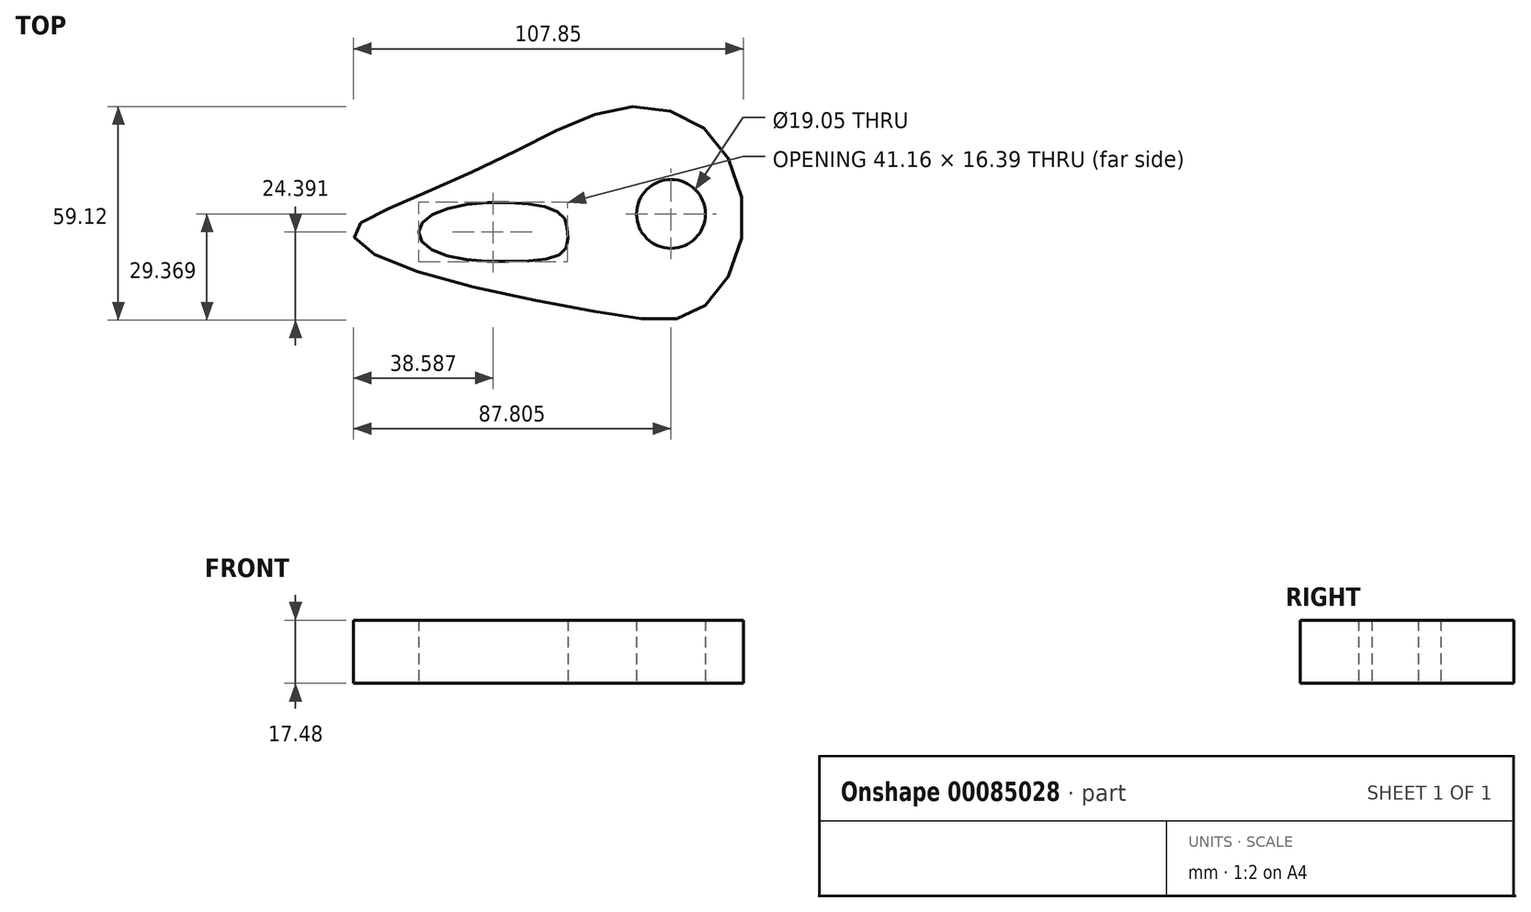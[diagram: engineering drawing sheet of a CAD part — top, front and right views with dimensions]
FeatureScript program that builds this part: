
annotation { "Feature Type Name" : "Feature", "Feature Type Description" : "" }
export const myFeature = defineFeature(function(context is Context, id is Id, definition is map)
    precondition{}
    {
        {
            var Q0;
            Q0=qCreatedBy(makeId("Top.planeOp"),FACE);
            var sketch = newSketch(context, id + "F0", { "sketchPlane" : qUnion([Q0])});
            skFitSpline(sketch, "E0", {"points": [v(-35.81, 6.55) * mm, v(0, 22.7) * mm, v(29.72, 34.6) * mm, v(53.19, 26.97) * mm, v(62.03, 0) * mm, v(49.53, -21.8) * mm, v(25.45, -22.7) * mm, v(-34.9, -8.38) * mm, v(-45.57, 0) * mm, v(-35.81, 6.55) * mm]});
            skSolve(sketch);
        }
        {
            var Q0;
            Q0=makeQuery(id+"F0.imprint","IMPRINT",FACE,{"disambiguationData":[TD([[makeQuery(id+"F0.imprint","IMPRINT",EDGE,{"derivedFrom":sQuery(id+"F0.wireOp",EDGE,"E0")}),-1.0]])]});
            extrude(context, id + "F1", {"entities" : qUnion([Q0]), "depth" : 17.48 * mm});
        }
        {
            var Q0;
            Q0=qCreatedBy(makeId("Top.planeOp"),FACE);
            var sketch = newSketch(context, id + "F2", { "sketchPlane" : qUnion([Q0])});
            skCircle(sketch, "E1", {"center": v(42.21, 5.03) * mm, "radius": 8.13 * mm});
            skSolve(sketch);
        }
        {
            var Q0;
            Q0=sQuery(id+"F2.wireOp",VERTEX,"E1.center");
            var Q1;
            Q1=makeQuery(id+"F1.opExtrude","SWEPT_BODY",BODY,{"disambiguationData":[OSD([sQuery(id+"F0.wireOp",EDGE,"E0")])]});
            hole(context, id + "F3", {"style" : HoleStyle.SIMPLE, "endStyle" : HoleEndStyle.THROUGH, "oppositeDirection" : true, "holeDiameter" : 19.05 * mm, "locations" : qUnion([Q0]), "scope" : qUnion([Q1]), "isTappedThrough" : true});
        }
        {
            var Q0;
            Q0=makeQuery(id+"F1.opExtrude","CAP_FACE",FACE,{"disambiguationData":[OSD([sQuery(id+"F0.wireOp",EDGE,"E0")])],"isStart":false});
            var sketch = newSketch(context, id + "F4", { "sketchPlane" : qUnion([Q0])});
            skFitSpline(sketch, "E2", {"points": [v(-27.58, 0) * mm, v(-22.1, 5.64) * mm, v(0, 8.08) * mm, v(12.04, 4.72) * mm, v(13.56, 0) * mm, v(12.65, -5.33) * mm, v(0, -8.08) * mm, v(-22.4, -5.64) * mm, v(-27.58, 0) * mm]});
            skSolve(sketch);
        }
        {
            var Q0;
            Q0=makeQuery(id+"F4.imprint","IMPRINT",FACE,{"disambiguationData":[TD([[makeQuery(id+"F4.imprint","IMPRINT",EDGE,{"derivedFrom":sQuery(id+"F4.wireOp",EDGE,"E2")}),-1.0]])]});
            extrude(context, id + "F5", {"entities" : qUnion([Q0]), "operationType" : NewBodyOperationType.REMOVE, "oppositeDirection" : true, "depth" : 25.4 * mm});
        }
    });
